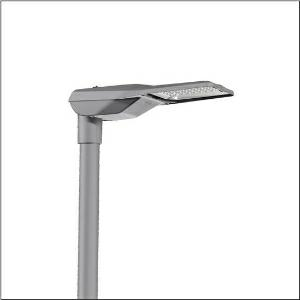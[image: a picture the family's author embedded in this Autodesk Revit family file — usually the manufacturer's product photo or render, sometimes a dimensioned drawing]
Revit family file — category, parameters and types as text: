
# Revit family: streetlight_sl_21_mini___stw1_0a_5xe2e43s08jb_a2c1
name_source: partatom
category: Lighting Fixtures
units: mm (PartAtom-declared; Revit-internal decimal feet)

## family parameters
Cut with Voids When Loaded = No
Host = Face
Light Source = No
Part Type = Normal
Room Calculation Point = No
Round Connector Dimension = Use Diameter
Shared = No

## types (1)
- --- (1 x LED, 13500 lm, 88.6 W, 4000K)
    Apparent Load = 89 VA
    CIE Flux Codes = 39 75 98 100 100
    Color Rendering = 70
    Color Temperature = 4000K
    Default Elevation = 1800 mm
    Description = Streetlight SL 21 mini, mast luminaire, primary light control with lens, of PMMA, primary optical cover: cover, of toughened safety glass, transparent, light distribution: STW1.0a, light emission: direct distribution, primary light characteristic: asymmetric, installation type: side-entry, post-top, LED, High Power LED, rated luminous flux: 13.500lm, luminous efficacy: 152lm/W, light colour: 740, colour temperature: 4000K, control gear: D4i, control: overheat protection, constant luminous flux control, time-dependent luminous flux control, flexible luminous flux parameterisation, pre-setting: logarithmic dimming characteristic, mains connection: 220..240V, AC, 50/60Hz, start of lifetime: 89W, end of service life: 92W, reduction: 41W, luminaire housing, of diecast aluminium, powder-coated, Siteco® metallic grey (DB 702S), corrosivity category C5 mid according to DIN EN ISO 12944, please order mast flange separately, inclination adjustable: 0°, 5°, 10°, 15°, sealing non-destructively replaceable, multi-level sealing system, length: 628mm, width: 235mm, height: 110mm, mast flange for spigot size: 42mm (side-entry): 5XC10008XM4, 60/48mm (side-entry/post-top): 5XC10108XM2, 76/60mm (side-entry/post-top): 5XC10108XM1, mounting height: 4..8m, Smart Interface above, protection rating (complete): IP66, insulation class (complete): insulation class II (safety insulation), certification: CE, ENEC, ENEC+, VDE, impact resistance: IK10, permissible operating ambient temperature for outdoor applications: -40..+50°C, standard-compliant lighting for roads and squares, packaging unit: 1 piece

Light Distribution: STW1.0a
    Height = 110 mm
    Lamp = 1 x LED
    Lamp Light Flux = 13500 lm
    Lamp Power = 88.6 W
    Lamp count = 1
    Length = 625 mm
    Luminous efficacy = 152 lm/W
    Manufacturer = Siteco
    ModVariant = No
    Model = 5XE2E43S08JB
    Number of Poles = 1
    OnlyDefault = Yes
    Power Factor = 1
    Product Name = Streetlight SL 21 mini | STW1.0a
    Product group = mast luminaire | pylon top
    ProductGroupID = 6100
    Protection Class = Protection class II
    Protection Degree = IP 66
    RLX_Detail_Level = 1
    RLX_Emergency_Light_Flux = 0 lm
    RLX_Emergency_Type = 0
    RLX_Emergency_Type_DB = No
    RlxData = <blob elided: 26281 chars, md5=73c283db>
    Socket = socket
    Standby Power = 0 W
    System Light Flux = 13500 lm
    System Power = 89 W
    Type Comments = factory setting: luminous flux: 100 % | dim-lin: 254 | 915 mA
    Type Image = l_1003515.jpg
    URL = http://relux.com
    VarID = @adj_031439
    Voltage = 0 V
    Weight = 0.00 kg
    Width = 234 mm

## geometry (parser evidence)
native form markers: Blend x4, Sweep x9
no freeform markers — native parametric forms only
